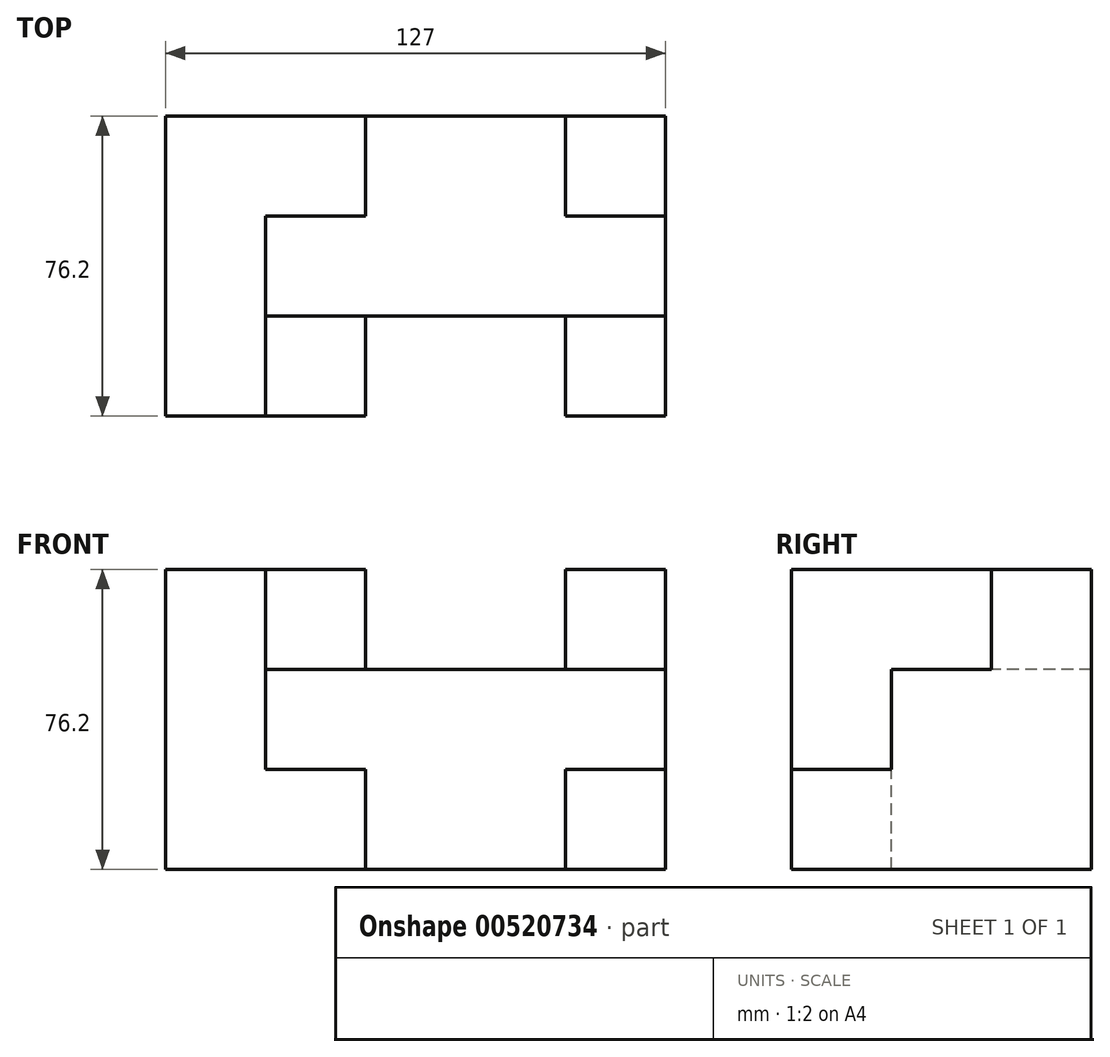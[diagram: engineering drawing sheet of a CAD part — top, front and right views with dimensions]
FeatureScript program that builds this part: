
annotation { "Feature Type Name" : "Feature", "Feature Type Description" : "" }
export const myFeature = defineFeature(function(context is Context, id is Id, definition is map)
    precondition{}
    {
        {
            var Q0;
            Q0=qCreatedBy(makeId("Front.planeOp"),FACE);
            var sketch = newSketch(context, id + "F0", { "sketchPlane" : qUnion([Q0])});
            skLineSegment(sketch, "E0.bottom", {"start": v(-63.86, 51.14) * mm, "end": v(63.14, 51.14) * mm});
            skLineSegment(sketch, "E0.top", {"start": v(-63.86, -25.06) * mm, "end": v(63.14, -25.06) * mm});
            skLineSegment(sketch, "E0.left", {"start": v(-63.86, 51.14) * mm, "end": v(-63.86, -25.06) * mm});
            skLineSegment(sketch, "E0.right", {"start": v(63.14, 51.14) * mm, "end": v(63.14, -25.06) * mm});
            skSolve(sketch);
        }
        {
            var Q0;
            Q0=makeQuery(id+"F0.imprint","IMPRINT",FACE,{"disambiguationData":[TD([[makeQuery(id+"F0.imprint","IMPRINT",EDGE,{"derivedFrom":sQuery(id+"F0.wireOp",EDGE,"E0.bottom")}),-1.0]])]});
            extrude(context, id + "F1", {"entities" : qUnion([Q0]), "depth" : 76.2 * mm, "offsetDistance" : 25.4 * mm});
        }
        {
            var Q0;
            Q0=makeQuery(id+"F1.opExtrude","SWEPT_FACE",FACE,{"disambiguationData":[OSD([sQuery(id+"F0.wireOp",EDGE,"E0.bottom")])]});
            var sketch = newSketch(context, id + "F2", { "sketchPlane" : qUnion([Q0])});
            skLineSegment(sketch, "E1.bottom", {"start": v(63.14, 0) * mm, "end": v(37.74, 0) * mm});
            skLineSegment(sketch, "E1.top", {"start": v(63.14, -25.4) * mm, "end": v(37.74, -25.4) * mm});
            skLineSegment(sketch, "E1.left", {"start": v(63.14, 0) * mm, "end": v(63.14, -25.4) * mm});
            skLineSegment(sketch, "E1.right", {"start": v(37.74, 0) * mm, "end": v(37.74, -25.4) * mm});
            skLineSegment(sketch, "E2.bottom", {"start": v(63.14, -76.2) * mm, "end": v(37.74, -76.2) * mm});
            skLineSegment(sketch, "E2.top", {"start": v(63.14, -50.8) * mm, "end": v(37.74, -50.8) * mm});
            skLineSegment(sketch, "E2.left", {"start": v(63.14, -76.2) * mm, "end": v(63.14, -50.8) * mm});
            skLineSegment(sketch, "E2.right", {"start": v(37.74, -76.2) * mm, "end": v(37.74, -50.8) * mm});
            skLineSegment(sketch, "E3", {"start": v(-63.86, -76.2) * mm, "end": v(-38.46, -76.2) * mm});
            skLineSegment(sketch, "E4", {"start": v(-38.46, -76.2) * mm, "end": v(-38.46, -25.4) * mm});
            skLineSegment(sketch, "E5", {"start": v(-38.46, -25.4) * mm, "end": v(-13.06, -25.4) * mm});
            skLineSegment(sketch, "E6", {"start": v(-13.06, -25.4) * mm, "end": v(-13.06, 0) * mm});
            skLineSegment(sketch, "E7.bottom", {"start": v(-38.46, -76.2) * mm, "end": v(-13.06, -76.2) * mm});
            skLineSegment(sketch, "E7.top", {"start": v(-38.46, -50.8) * mm, "end": v(-13.06, -50.8) * mm});
            skLineSegment(sketch, "E7.left", {"start": v(-38.46, -76.2) * mm, "end": v(-38.46, -50.8) * mm});
            skLineSegment(sketch, "E7.right", {"start": v(-13.06, -76.2) * mm, "end": v(-13.06, -50.8) * mm});
            skLineSegment(sketch, "E8", {"start": v(-13.06, -50.8) * mm, "end": v(37.74, -50.8) * mm});
            skSolve(sketch);
        }
        {
            var Q0;
            {var subQ0=sQuery(id+"F2.wireOp",EDGE,"E2.right");Q0=makeQuery(id+"F2.imprint","IMPRINT",FACE,{"disambiguationData":[TD([[makeQuery(id+"F2.imprint","IMPRINT",EDGE,{"derivedFrom":subQ0}),1.0]])]});}
            extrude(context, id + "F3", {"entities" : qUnion([Q0]), "operationType" : NewBodyOperationType.REMOVE, "oppositeDirection" : true, "depth" : 76.2 * mm, "offsetDistance" : 25.4 * mm});
        }
        {
            var Q0;
            Q0=makeQuery(id+"F2.imprint","IMPRINT",FACE,{"disambiguationData":[TD([[makeQuery(id+"F2.imprint","IMPRINT",EDGE,{"derivedFrom":sQuery(id+"F2.wireOp",EDGE,"E7.bottom")}),1.0]])]});
            var Q1;
            Q1=makeQuery(id+"F2.imprint","IMPRINT",FACE,{"disambiguationData":[TD([[makeQuery(id+"F2.imprint","IMPRINT",EDGE,{"derivedFrom":sQuery(id+"F2.wireOp",EDGE,"E2.bottom")}),1.0]])]});
            extrude(context, id + "F4", {"entities" : qUnion([Q0, Q1]), "operationType" : NewBodyOperationType.REMOVE, "oppositeDirection" : true, "depth" : 50.8 * mm, "offsetDistance" : 25.4 * mm});
        }
        {
            var Q0;
            {var subQ2=sQuery(id+"F2.wireOp",EDGE,"E1.top");Q0=makeQuery(id+"F2.imprint","IMPRINT",FACE,{"disambiguationData":[TD([[makeQuery(id+"F2.imprint","IMPRINT",EDGE,{"derivedFrom":subQ2}),1.0]])]});}
            extrude(context, id + "F5", {"entities" : qUnion([Q0]), "operationType" : NewBodyOperationType.REMOVE, "oppositeDirection" : true, "depth" : 25.4 * mm, "offsetDistance" : 25.4 * mm});
        }
    });
